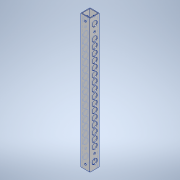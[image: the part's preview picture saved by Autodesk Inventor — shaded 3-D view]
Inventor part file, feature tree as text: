
AUTODESK INVENTOR PART (.ipt)
format: ipt  version: 2020.3 (Build 243373000, 373)  size: 184,832 bytes
history: native  units: mm
features: sketch x4, hole x3, other x1, extrude x1
ambient origin geometry x8: Origin, YZ Plane, XZ Plane, XY Plane, X Axis, Y Axis, Z Axis, Center Point
bodies: Body1 (feature_tree)
feature tree (9):
  other  "ソリッド1"
  extrude  "押し出し1"  Depth=15.0mm
  hole  "穴1"  [1 undecoded]
  hole  "穴2"  [1 undecoded]
  hole  "穴3"  [1 undecoded]
  sketch  "スケッチ1"
  sketch  "スケッチ2"
  sketch  "スケッチ3"
  sketch  "スケッチ4"
note: 3 required parameter values undecoded (feature->parameter linkage not recoverable at this tier; creation-order binding heuristic only, values carry confidence <= 0.55)
